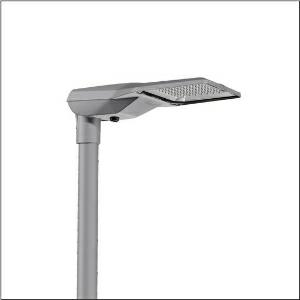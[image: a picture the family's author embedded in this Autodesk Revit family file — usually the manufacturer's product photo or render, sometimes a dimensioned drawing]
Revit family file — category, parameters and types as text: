
# Revit family: streetlight_sl_21_iq_midi___p0_8a_5xe3u31u08mb_6097
name_source: partatom
category: Lighting Fixtures
units: mm (PartAtom-declared; Revit-internal decimal feet)

## family parameters
Cut with Voids When Loaded = No
Host = Face
Light Source = No
Part Type = Normal
Room Calculation Point = No
Round Connector Dimension = Use Diameter
Shared = No

## types (1)
- --- (1 x LED, 18500 lm, 129.3 W, 3000K)
    Apparent Load = 129 VA
    CIE Flux Codes = 33 69 96 100 100
    Color Rendering = 70
    Color Temperature = 3000K
    Default Elevation = 1800 mm
    Description = Streetlight SL 21 iQ midi, mast luminaire, primary light control with lens, of PMMA, primary optical cover: cover, of toughened safety glass, transparent, light distribution: P0.8a, light emission: direct distribution, primary light characteristic: asymmetric, installation type: post-top, side-entry, LED, High Power LED, rated luminous flux: 18.500lm, luminous efficacy: 143lm/W, light colour: 730, colour temperature: 3000K, control gear: iQ-Street Remote, D4i with power reduction, control: pre-setting: logarithmic dimming characteristic, Street-Remote, Auto-Match, Temp-Guard, Lumen-Switch, Night-Set, Smart-Wire, Light-Fading, Desk-Remote (wireless, voltage-free reading and setting of iQ features in the workshop via application-optimized NFC function/RFID function), optimised constant luminous flux control (CLO 2.0), mains connection: 230..240V, AC, 50/60Hz, start of lifetime: 129W, end of service life: 142W, reduction: 56W, luminaire housing, of diecast aluminium, powder-coated, SITECO metallic grey (DB 702S), corrosivity category C5 high according to DIN EN ISO 12944, please order mast flange separately, inclination adjustable: 0°, 5°, 10°, 15°, sealing non-destructively replaceable, multi-level sealing system, length: 644mm, width: 335mm, height: 110mm, mast flange for spigot size: 42mm (side-entry): 5XC10008XM4, 60/48mm (side-entry/post-top): 5XC10108XM2, 76/60mm (side-entry/post-top): 5XC10108XM1, mounting height: 4..8m, Smart Interface below, protection rating (complete): IP66, insulation class (complete): insulation class II (safety insulation), certification: CE, ENEC, ENEC+, VDE, impact resistance: IK10, permissible operating ambient temperature for outdoor applications: -40..+50°C, standard-compliant lighting for roads and squares, packaging unit: 1 piece

Light Distribution: P0.8a
    Height = 111 mm
    Lamp = 1 x LED
    Lamp Light Flux = 18500 lm
    Lamp Power = 129.3 W
    Lamp count = 1
    Length = 644 mm
    Luminous efficacy = 143 lm/W
    Manufacturer = Siteco
    ModVariant = No
    Model = 5XE3U31U08MB
    Number of Poles = 1
    OnlyDefault = Yes
    Power Factor = 1
    Product Name = Streetlight SL 21 iQ midi | P0.8a
    Product group = mast luminaire | pylon top
    ProductGroupID = 6100
    Protection Class = Protection class II
    Protection Degree = IP 66
    RLX_Detail_Level = 1
    RLX_Emergency_Light_Flux = 0 lm
    RLX_Emergency_Type = 0
    RLX_Emergency_Type_DB = No
    RlxData = <blob elided: 91229 chars, md5=a61cea52>
    Socket = socket
    Standby Power = 0 W
    System Light Flux = 18500 lm
    System Power = 129 W
    Type Comments = factory setting: luminous flux: 100 % | dim-lin: 254 | 672 mA
    Type Image = l_1004300.jpg
    URL = http://relux.com
    VarID = @adj_081725
    Voltage = 0 V
    Weight = 0.00 kg
    Width = 336 mm

## geometry (parser evidence)
native form markers: Blend x4, Sweep x10
no freeform markers — native parametric forms only
